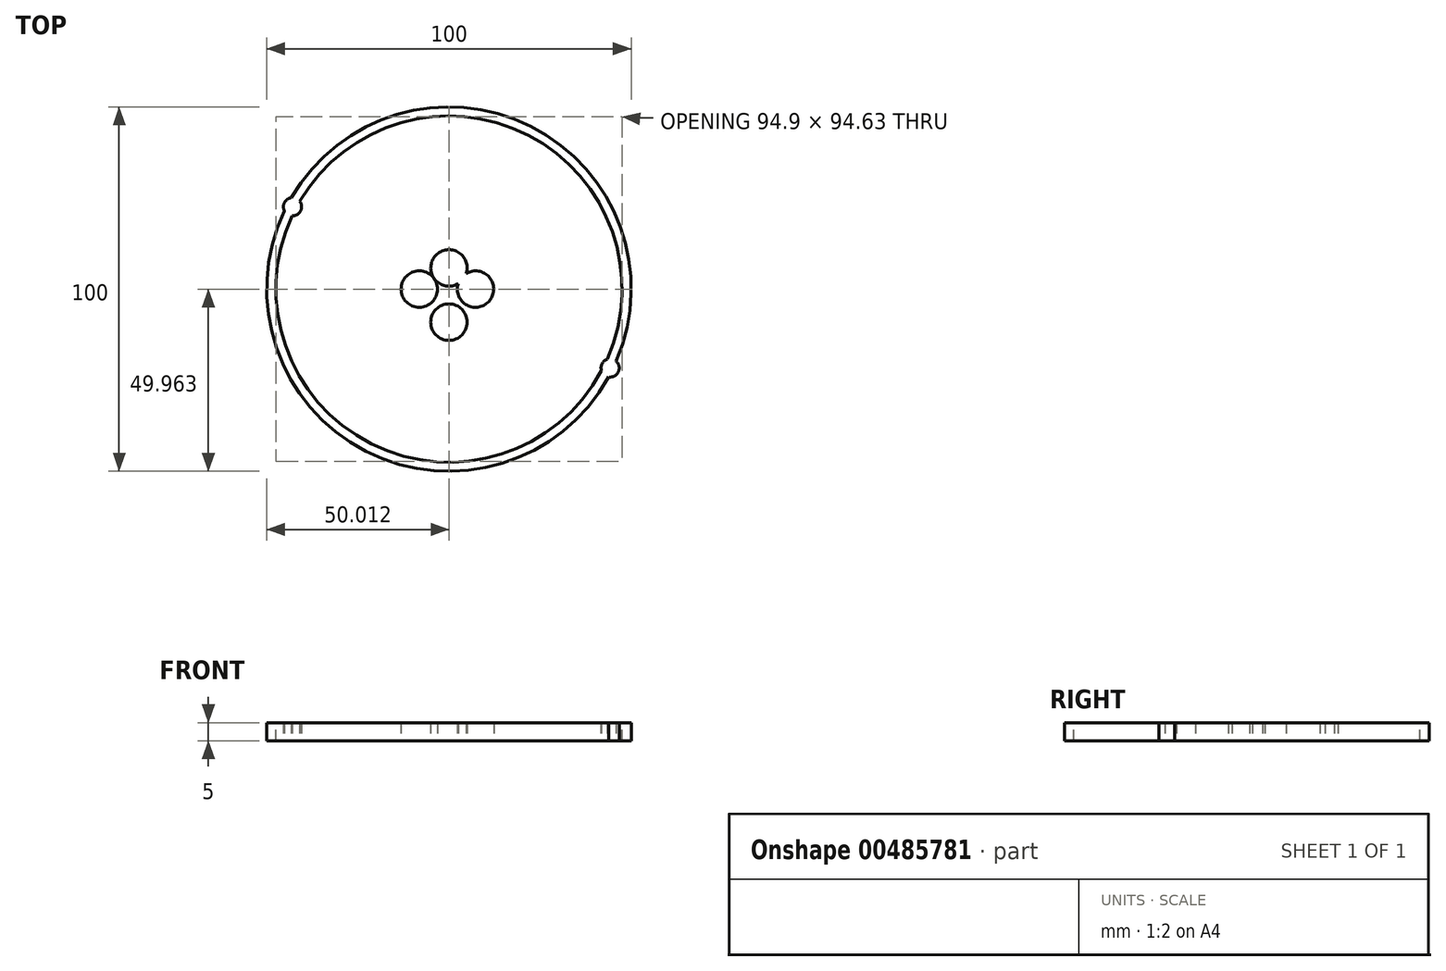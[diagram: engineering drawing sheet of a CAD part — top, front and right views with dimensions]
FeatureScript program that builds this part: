
annotation { "Feature Type Name" : "Feature", "Feature Type Description" : "" }
export const myFeature = defineFeature(function(context is Context, id is Id, definition is map)
    precondition{}
    {
        {
            var Q0;
            Q0=qCreatedBy(makeId("Top.planeOp"),FACE);
            var sketch = newSketch(context, id + "F0", { "sketchPlane" : qUnion([Q0])});
            skCircle(sketch, "E0", {"center": v(0, 0) * mm, "radius": 50 * mm});
            skSolve(sketch);
        }
        {
            var Q0;
            Q0=makeQuery(id+"F0.imprint","IMPRINT",FACE,{"disambiguationData":[TD([[makeQuery(id+"F0.imprint","IMPRINT",EDGE,{"derivedFrom":sQuery(id+"F0.wireOp",EDGE,"E0")}),1.0]])]});
            extrude(context, id + "F1", {"entities" : qUnion([Q0]), "depth" : 5 * mm});
        }
        {
            var Q0;
            Q0=makeQuery(id+"F1.opExtrude","CAP_FACE",FACE,{"disambiguationData":[OSD([sQuery(id+"F0.wireOp",EDGE,"E0")])],"isStart":false});
            var sketch = newSketch(context, id + "F2", { "sketchPlane" : qUnion([Q0])});
            skCircle(sketch, "E1", {"center": v(0, 0) * mm, "radius": 47.5 * mm});
            skSolve(sketch);
        }
        {
            var Q0;
            Q0 = qSketchRegion(id + "F2", true);
            extrude(context, id + "F3", {"entities" : qUnion([Q0]), "operationType" : NewBodyOperationType.REMOVE, "oppositeDirection" : true, "depth" : 5 * mm});
        }
        {
            var Q0;
            Q0=qCreatedBy(makeId("Top.planeOp"),FACE);
            var sketch = newSketch(context, id + "F4", { "sketchPlane" : qUnion([Q0])});
            skCircle(sketch, "E2", {"center": v(-8.14, 0) * mm, "radius": 5 * mm});
            skCircle(sketch, "E3", {"center": v(7.28, 0) * mm, "radius": 5 * mm});
            skCircle(sketch, "E4", {"center": v(0, 5.81) * mm, "radius": 5 * mm});
            skCircle(sketch, "E5", {"center": v(0, -9.08) * mm, "radius": 5 * mm});
            skSolve(sketch);
        }
        {
            var Q0;
            {var subQ0=sQuery(id+"F4.wireOp",EDGE,"E4");var subQ1=sQuery(id+"F4.wireOp",EDGE,"E3");var subQ2=makeQuery(id+"F4.imprint","INTERSECT",VERTEX,{"disambiguationData":[OD(0.0)],"derivedFrom":[subQ1,subQ0]});Q0=makeQuery(id+"F4.imprint","IMPRINT",FACE,{"disambiguationData":[TD([[makeQuery(id+"F4.imprint","IMPRINT",EDGE,{"disambiguationData":[TD([[subQ2,1.0]])],"derivedFrom":subQ1}),1.0]])]});}
            var Q1;
            {var subQ0=sQuery(id+"F4.wireOp",EDGE,"E4");var subQ1=sQuery(id+"F4.wireOp",EDGE,"E3");var subQ2=makeQuery(id+"F4.imprint","INTERSECT",VERTEX,{"disambiguationData":[OD(0.0)],"derivedFrom":[subQ1,subQ0]});Q1=makeQuery(id+"F4.imprint","IMPRINT",FACE,{"disambiguationData":[TD([[makeQuery(id+"F4.imprint","IMPRINT",EDGE,{"disambiguationData":[TD([[subQ2,-1.0]])],"derivedFrom":subQ1}),1.0]])]});}
            var Q2;
            {var subQ0=sQuery(id+"F4.wireOp",EDGE,"E4");var subQ1=sQuery(id+"F4.wireOp",EDGE,"E3");var subQ2=makeQuery(id+"F4.imprint","INTERSECT",VERTEX,{"disambiguationData":[OD(0.0)],"derivedFrom":[subQ1,subQ0]});Q2=makeQuery(id+"F4.imprint","IMPRINT",FACE,{"disambiguationData":[TD([[makeQuery(id+"F4.imprint","IMPRINT",EDGE,{"disambiguationData":[TD([[subQ2,1.0]])],"derivedFrom":subQ1}),-1.0]])]});}
            var Q3;
            Q3=makeQuery(id+"F4.imprint","IMPRINT",FACE,{"disambiguationData":[TD([[makeQuery(id+"F4.imprint","IMPRINT",EDGE,{"derivedFrom":sQuery(id+"F4.wireOp",EDGE,"E2")}),1.0]])]});
            var Q4;
            Q4=makeQuery(id+"F4.imprint","IMPRINT",FACE,{"disambiguationData":[TD([[makeQuery(id+"F4.imprint","IMPRINT",EDGE,{"derivedFrom":sQuery(id+"F4.wireOp",EDGE,"E5")}),1.0]])]});
            extrude(context, id + "F5", {"entities" : qUnion([Q0, Q1, Q2, Q3, Q4]), "depth" : 5 * mm});
        }
        {
            var Q0;
            Q0=qCreatedBy(makeId("Top.planeOp"),FACE);
            var sketch = newSketch(context, id + "F6", { "sketchPlane" : qUnion([Q0])});
            skCircle(sketch, "E6", {"center": v(-42.94, 22.58) * mm, "radius": 2.5 * mm});
            skCircle(sketch, "E7", {"center": v(44.23, -21.64) * mm, "radius": 2.5 * mm});
            skSolve(sketch);
        }
        {
            var Q0;
            Q0=makeQuery(id+"F6.imprint","IMPRINT",FACE,{"disambiguationData":[TD([[makeQuery(id+"F6.imprint","IMPRINT",EDGE,{"derivedFrom":sQuery(id+"F6.wireOp",EDGE,"E6")}),1.0]])]});
            var Q1;
            Q1=makeQuery(id+"F6.imprint","IMPRINT",FACE,{"disambiguationData":[TD([[makeQuery(id+"F6.imprint","IMPRINT",EDGE,{"derivedFrom":sQuery(id+"F6.wireOp",EDGE,"E7")}),1.0]])]});
            extrude(context, id + "F7", {"entities" : qUnion([Q0, Q1]), "operationType" : NewBodyOperationType.ADD, "depth" : 5 * mm});
        }
    });
